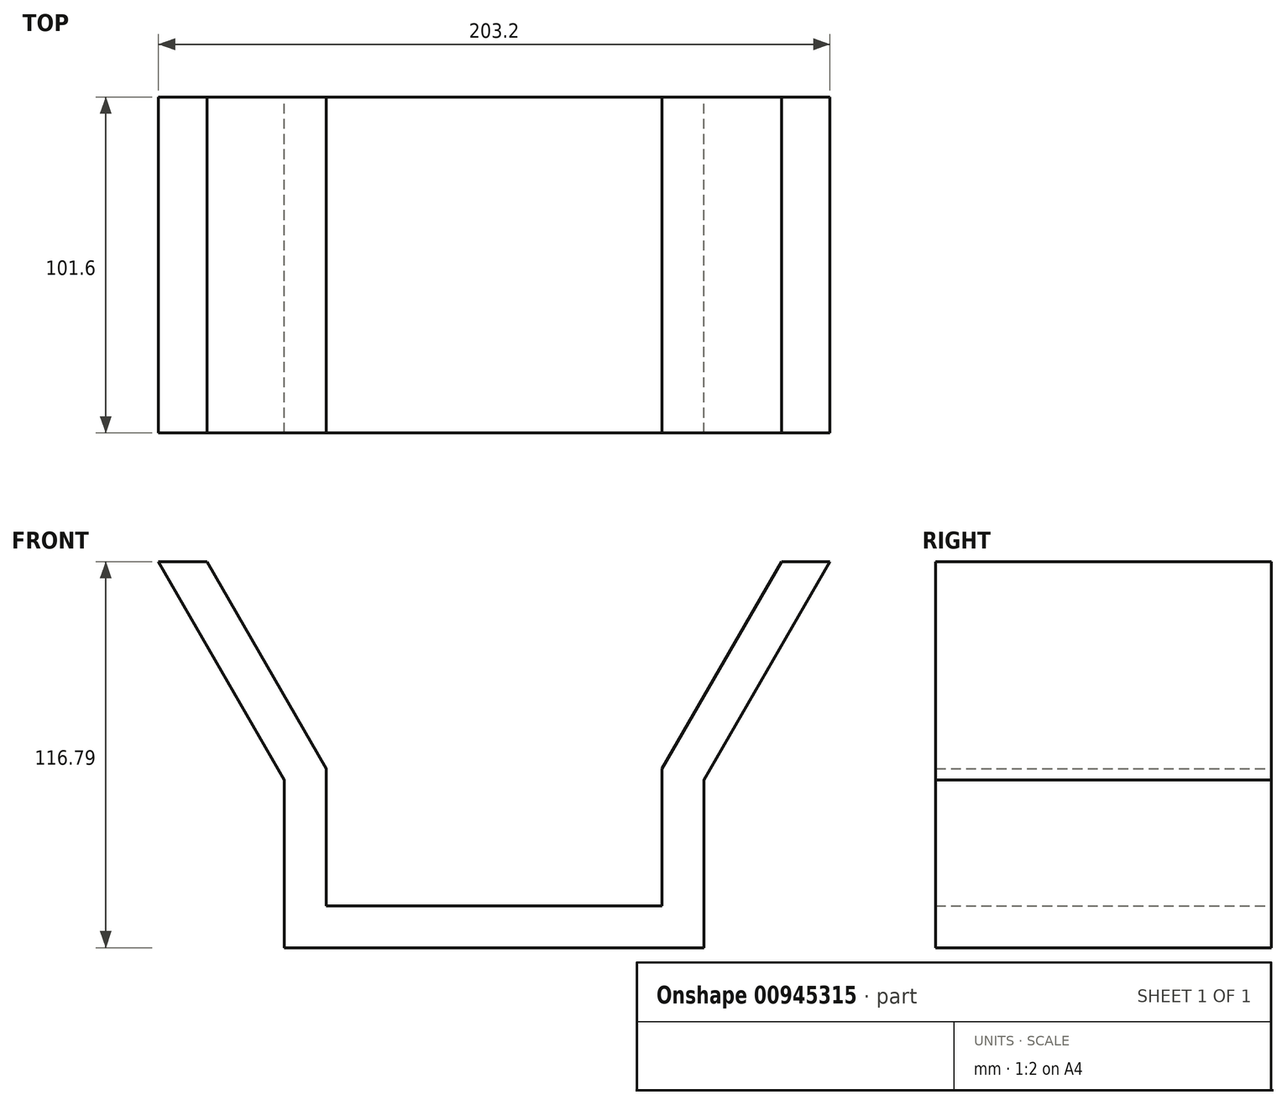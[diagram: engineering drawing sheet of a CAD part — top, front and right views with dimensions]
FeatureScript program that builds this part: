
annotation { "Feature Type Name" : "Feature", "Feature Type Description" : "" }
export const myFeature = defineFeature(function(context is Context, id is Id, definition is map)
    precondition{}
    {
        {
            var Q0;
            Q0=qCreatedBy(makeId("Front.planeOp"),FACE);
            var sketch = newSketch(context, id + "F0", { "sketchPlane" : qUnion([Q0])});
            skLineSegment(sketch, "E0", {"start": v(0, -50.8) * mm, "end": v(-63.5, -50.8) * mm});
            skLineSegment(sketch, "E1", {"start": v(-63.5, -50.8) * mm, "end": v(-63.5, 0) * mm});
            skLineSegment(sketch, "E2", {"start": v(-63.5, 0) * mm, "end": v(-101.6, 66) * mm});
            skLineSegment(sketch, "E3", {"start": v(-101.6, 66) * mm, "end": v(-86.94, 66) * mm});
            skLineSegment(sketch, "E4", {"start": v(-86.94, 66) * mm, "end": v(-50.8, 3.4) * mm});
            skLineSegment(sketch, "E5", {"start": v(-50.8, -38.1) * mm, "end": v(0, -38.1) * mm});
            skLineSegment(sketch, "E6", {"start": v(-50.8, -38.1) * mm, "end": v(-50.8, 3.4) * mm});
            skLineSegment(sketch, "E7", {"start": v(0, 0) * mm, "end": v(0, -50.8) * mm, "construction": true});
            skLineSegment(sketch, "E8.MirrorCS", {"start": v(50.8, -38.1) * mm, "end": v(0, -38.1) * mm});
            skLineSegment(sketch, "E9.MirrorCS", {"start": v(50.8, -38.1) * mm, "end": v(50.8, 3.4) * mm});
            skLineSegment(sketch, "E10.MirrorCS", {"start": v(86.94, 66) * mm, "end": v(50.8, 3.4) * mm});
            skLineSegment(sketch, "E11.MirrorCS", {"start": v(101.6, 66) * mm, "end": v(86.94, 66) * mm});
            skLineSegment(sketch, "E12.MirrorCS", {"start": v(63.5, 0) * mm, "end": v(101.6, 66) * mm});
            skLineSegment(sketch, "E13.MirrorCS", {"start": v(63.5, -50.8) * mm, "end": v(63.5, 0) * mm});
            skLineSegment(sketch, "E14.MirrorCS", {"start": v(0, -50.8) * mm, "end": v(63.5, -50.8) * mm});
            skSolve(sketch);
        }
        {
            var Q0;
            Q0=makeQuery(id+"F0.imprint","IMPRINT",FACE,{"disambiguationData":[TD([[makeQuery(id+"F0.imprint","IMPRINT",EDGE,{"derivedFrom":sQuery(id+"F0.wireOp",EDGE,"E0")}),-1.0]])]});
            extrude(context, id + "F1", {"entities" : qUnion([Q0]), "endBound" : BoundingType.SYMMETRIC, "depth" : 101.6 * mm, "offsetDistance" : 25.4 * mm});
        }
        {
            var Q0;
            Q0=qCreatedBy(makeId("Right.planeOp"),FACE);
            var sketch = newSketch(context, id + "F2", { "sketchPlane" : qUnion([Q0])});
            skLineSegment(sketch, "E15", {"start": v(0, -49.38) * mm, "end": v(-63.5, -49.38) * mm});
            skLineSegment(sketch, "E16", {"start": v(-63.5, -49.38) * mm, "end": v(-63.5, 1.42) * mm});
            skLineSegment(sketch, "E17", {"start": v(-63.5, 1.42) * mm, "end": v(-101.6, 67.41) * mm});
            skLineSegment(sketch, "E18", {"start": v(-101.6, 67.41) * mm, "end": v(-86.94, 67.41) * mm});
            skLineSegment(sketch, "E19", {"start": v(-86.94, 67.41) * mm, "end": v(-50.8, 4.82) * mm});
            skLineSegment(sketch, "E20", {"start": v(-50.8, -36.68) * mm, "end": v(0, -36.68) * mm});
            skLineSegment(sketch, "E21", {"start": v(-50.8, -36.68) * mm, "end": v(-50.8, 4.82) * mm});
            skLineSegment(sketch, "E22", {"start": v(0, 1.42) * mm, "end": v(0, -49.38) * mm, "construction": true});
            skLineSegment(sketch, "E23.MirrorCS", {"start": v(50.8, -36.68) * mm, "end": v(0, -36.68) * mm});
            skLineSegment(sketch, "E24.MirrorCS", {"start": v(50.8, -36.68) * mm, "end": v(50.8, 4.82) * mm});
            skLineSegment(sketch, "E25.MirrorCS", {"start": v(86.94, 67.41) * mm, "end": v(50.8, 4.82) * mm});
            skLineSegment(sketch, "E26.MirrorCS", {"start": v(101.6, 67.41) * mm, "end": v(86.94, 67.41) * mm});
            skLineSegment(sketch, "E27.MirrorCS", {"start": v(63.5, 1.42) * mm, "end": v(101.6, 67.41) * mm});
            skLineSegment(sketch, "E28.MirrorCS", {"start": v(63.5, -49.38) * mm, "end": v(63.5, 1.42) * mm});
            skLineSegment(sketch, "E29.MirrorCS", {"start": v(0, -49.38) * mm, "end": v(63.5, -49.38) * mm});
            skSolve(sketch);
        }
        {
            var Q0;
            Q0=sQuery(id+"F2.wireOp",EDGE,"E23.MirrorCS");
            var Q1;
            Q1=sQuery(id+"F2.wireOp",EDGE,"E25.MirrorCS");
            var Q2;
            Q2=sQuery(id+"F2.wireOp",EDGE,"E29.MirrorCS");
            var Q3;
            Q3=sQuery(id+"F2.wireOp",EDGE,"E26.MirrorCS");
            var Q4;
            Q4=sQuery(id+"F2.wireOp",EDGE,"E18");
            var Q5;
            Q5=sQuery(id+"F2.wireOp",EDGE,"E16");
            var Q6;
            Q6=sQuery(id+"F2.wireOp",EDGE,"E28.MirrorCS");
            var Q7;
            Q7=sQuery(id+"F2.wireOp",EDGE,"E17");
            var Q8;
            Q8=sQuery(id+"F2.wireOp",EDGE,"E27.MirrorCS");
            var Q9;
            Q9=sQuery(id+"F2.wireOp",EDGE,"E15");
            var Q10;
            Q10=sQuery(id+"F2.wireOp",EDGE,"E24.MirrorCS");
            var Q11;
            Q11=sQuery(id+"F2.wireOp",EDGE,"E19");
            var Q12;
            Q12=sQuery(id+"F2.wireOp",EDGE,"E20");
            var Q13;
            Q13=sQuery(id+"F2.wireOp",EDGE,"E21");
            extrude(context, id + "F3", {"bodyType" : ToolBodyType.SURFACE, "surfaceEntities" : qUnion([Q0, Q1, Q2, Q3, Q4, Q5, Q6, Q7, Q8, Q9, Q10, Q11, Q12, Q13]), "endBound" : BoundingType.SYMMETRIC, "depth" : 127 * mm, "offsetDistance" : 25.4 * mm});
        }
    });
